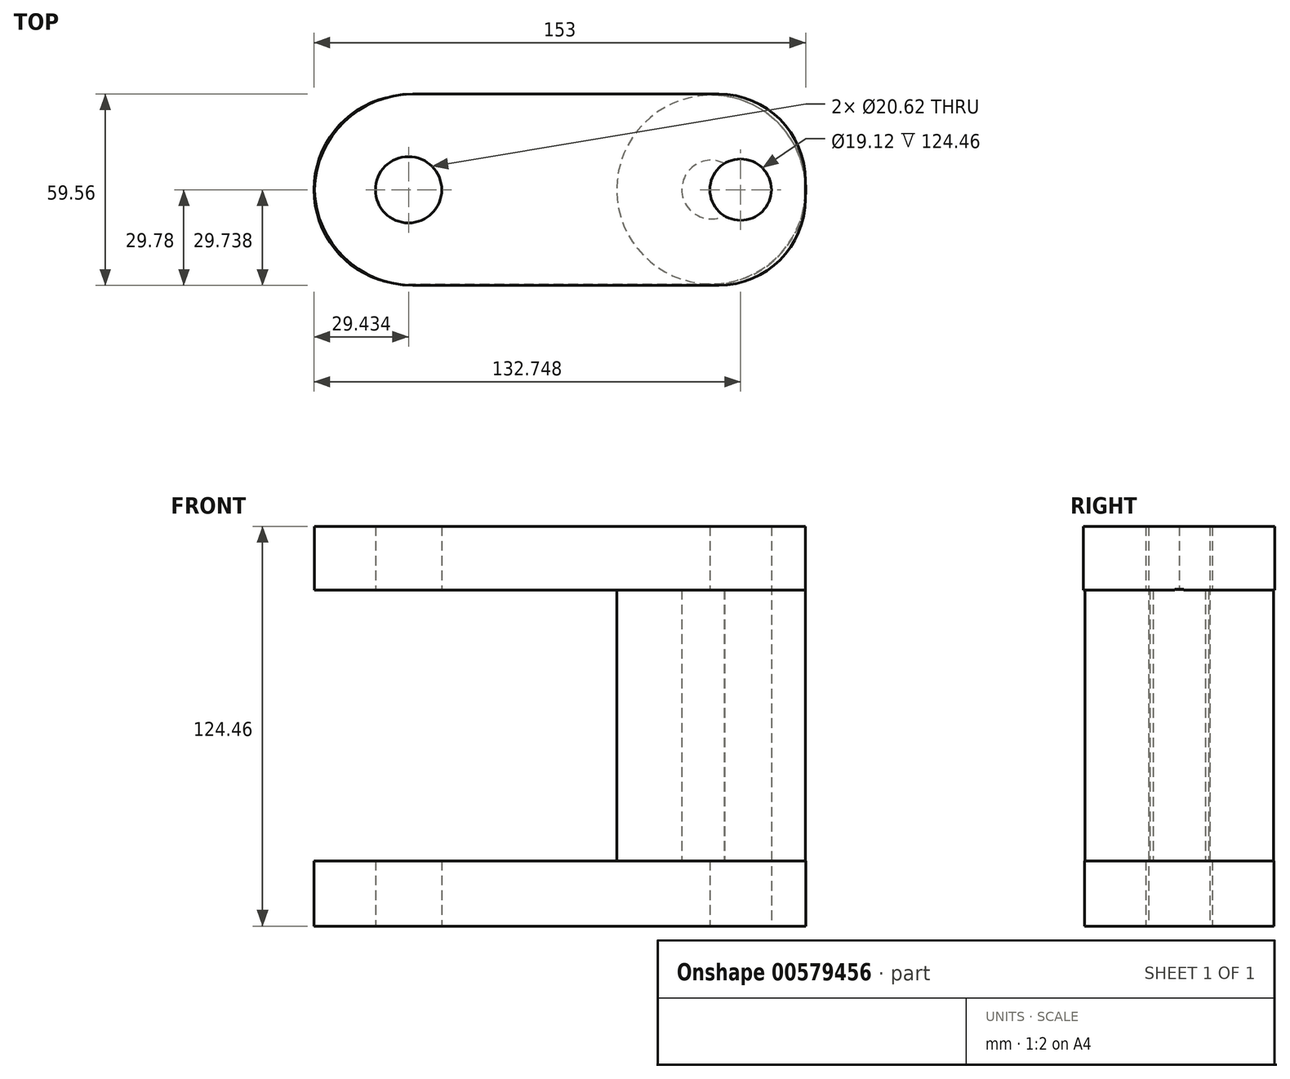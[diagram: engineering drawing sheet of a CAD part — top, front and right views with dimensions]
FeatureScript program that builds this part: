
annotation { "Feature Type Name" : "Feature", "Feature Type Description" : "" }
export const myFeature = defineFeature(function(context is Context, id is Id, definition is map)
    precondition{}
    {
        {
            var Q0;
            Q0=qCreatedBy(makeId("Top.planeOp"),FACE);
            var sketch = newSketch(context, id + "F0", { "sketchPlane" : qUnion([Q0])});
            skLineSegment(sketch, "E0.bottom", {"start": v(76.5, 29.48) * mm, "end": v(-76.5, 29.48) * mm});
            skLineSegment(sketch, "E0.top", {"start": v(76.5, -29.48) * mm, "end": v(-76.5, -29.48) * mm});
            skLineSegment(sketch, "E0.left", {"start": v(76.5, 29.48) * mm, "end": v(76.5, -29.48) * mm});
            skLineSegment(sketch, "E0.right", {"start": v(-76.5, 29.48) * mm, "end": v(-76.5, -29.48) * mm});
            skPoint(sketch, "E0.middle", {"position": v(0, 0) * mm});
            skSolve(sketch);
        }
        {
            var Q0;
            Q0 = qSketchRegion(id + "F0", true);
            extrude(context, id + "F1", {"entities" : qUnion([Q0]), "depth" : 20.32 * mm, "offsetDistance" : 25.4 * mm});
        }
        {
            var Q0;
            Q0=makeQuery(id+"F1.opExtrude","SWEPT_EDGE",EDGE,{"disambiguationData":[OSD([sQuery(id+"F0.wireOp",EDGE,"E0.top"),sQuery(id+"F0.wireOp",EDGE,"E0.right")])]});
            var Q1;
            Q1=makeQuery(id+"F1.opExtrude","SWEPT_EDGE",EDGE,{"disambiguationData":[OSD([sQuery(id+"F0.wireOp",EDGE,"E0.bottom"),sQuery(id+"F0.wireOp",EDGE,"E0.right")])]});
            var Q2;
            Q2=makeQuery(id+"F1.opExtrude","SWEPT_EDGE",EDGE,{"disambiguationData":[OSD([sQuery(id+"F0.wireOp",EDGE,"E0.top"),sQuery(id+"F0.wireOp",EDGE,"E0.left")])]});
            var Q3;
            Q3=makeQuery(id+"F1.opExtrude","SWEPT_EDGE",EDGE,{"disambiguationData":[OSD([sQuery(id+"F0.wireOp",EDGE,"E0.bottom"),sQuery(id+"F0.wireOp",EDGE,"E0.left")])]});
            fillet(context, id + "F2", {"entities" : qUnion([Q0, Q1, Q2, Q3]), "radius" : 29.43 * mm, "tangentPropagation" : true, "allowEdgeOverflow" : false});
        }
        {
            var Q0;
            Q0=makeQuery(id+"F1.opExtrude","CAP_FACE",FACE,{"disambiguationData":[OSD([sQuery(id+"F0.wireOp",EDGE,"E0.bottom"),sQuery(id+"F0.wireOp",EDGE,"E0.top"),sQuery(id+"F0.wireOp",EDGE,"E0.left"),sQuery(id+"F0.wireOp",EDGE,"E0.right")])],"isStart":false});
            var sketch = newSketch(context, id + "F3", { "sketchPlane" : qUnion([Q0])});
            skCircle(sketch, "E1", {"center": v(47.07, 0.04) * mm, "radius": 29.37 * mm});
            skCircle(sketch, "E2", {"center": v(47.07, 0.04) * mm, "radius": 9.12 * mm});
            skSolve(sketch);
        }
        {
            var Q0;
            Q0=makeQuery(id+"F3.imprint","IMPRINT",FACE,{"disambiguationData":[TD([[makeQuery(id+"F3.imprint","IMPRINT",EDGE,{"derivedFrom":sQuery(id+"F3.wireOp",EDGE,"E1")}),1.0]])]});
            extrude(context, id + "F4", {"entities" : qUnion([Q0]), "operationType" : NewBodyOperationType.ADD, "depth" : 84.58 * mm, "offsetDistance" : 25.4 * mm});
        }
        {
            var Q0;
            Q0=makeQuery(id+"F4.boolean.opBoolean","SPLIT",FACE,{"disambiguationData":[TD([makeQuery(id+"F4.opExtrude","SWEPT_FACE",FACE,{"disambiguationData":[OSD([sQuery(id+"F3.wireOp",EDGE,"E2")])]})])],"derivedFrom":makeQuery(id+"F1.opExtrude","CAP_FACE",FACE,{"disambiguationData":[OSD([sQuery(id+"F0.wireOp",EDGE,"E0.bottom"),sQuery(id+"F0.wireOp",EDGE,"E0.top"),sQuery(id+"F0.wireOp",EDGE,"E0.left"),sQuery(id+"F0.wireOp",EDGE,"E0.right")])],"isStart":false})});
            extrude(context, id + "F5", {"entities" : qUnion([Q0]), "operationType" : NewBodyOperationType.REMOVE, "endBound" : BoundingType.THROUGH_ALL, "depth" : 25.4 * mm, "offsetDistance" : 25.4 * mm});
        }
        {
            var Q0;
            {var subQ0=sQuery(id+"F0.wireOp",EDGE,"E0.left");var subQ1=sQuery(id+"F0.wireOp",EDGE,"E0.bottom");var subQ2=sQuery(id+"F0.wireOp",EDGE,"E0.top");var subQ3=sQuery(id+"F0.wireOp",EDGE,"E0.right");Q0=makeQuery(id+"F4.boolean.opBoolean","SPLIT",FACE,{"disambiguationData":[TD([makeQuery(id+"F1.opExtrude","SWEPT_FACE",FACE,{"disambiguationData":[OSD([subQ1])]})])],"derivedFrom":makeQuery(id+"F1.opExtrude","CAP_FACE",FACE,{"disambiguationData":[OSD([subQ1,subQ2,subQ0,subQ3])],"isStart":false})});}
            var sketch = newSketch(context, id + "F6", { "sketchPlane" : qUnion([Q0])});
            skCircle(sketch, "E3", {"center": v(-47.07, 0.04) * mm, "radius": 12.08 * mm});
            skSolve(sketch);
        }
        {
            var Q0;
            Q0=makeQuery(id+"F6.imprint","IMPRINT",FACE,{"disambiguationData":[TD([[makeQuery(id+"F6.imprint","IMPRINT",EDGE,{"derivedFrom":sQuery(id+"F6.wireOp",EDGE,"E3")}),1.0]])]});
            extrude(context, id + "F7", {"entities" : qUnion([Q0]), "operationType" : NewBodyOperationType.REMOVE, "endBound" : BoundingType.THROUGH_ALL, "depth" : 25.4 * mm, "offsetDistance" : 25.4 * mm});
        }
        {
            var Q0;
            Q0=qCreatedBy(makeId("Top.planeOp"),FACE);
            cPlane(context, id + "F8", {"entities" : qUnion([Q0]), "cplaneType" : CPlaneType.OFFSET, "offset" : 104.65 * mm, "width" : 152.4 * mm, "height" : 152.4 * mm});
        }
        {
            var Q0;
            Q0=qCreatedBy(id+"F8.planeOp",FACE);
            var sketch = newSketch(context, id + "F9", { "sketchPlane" : qUnion([Q0])});
            skLineSegment(sketch, "E4.bottom", {"start": v(76.4, -29.78) * mm, "end": v(-76.4, -29.78) * mm});
            skLineSegment(sketch, "E4.top", {"start": v(76.4, 29.78) * mm, "end": v(-76.4, 29.78) * mm});
            skLineSegment(sketch, "E4.left", {"start": v(76.4, -29.78) * mm, "end": v(76.4, 29.78) * mm});
            skLineSegment(sketch, "E4.right", {"start": v(-76.4, -29.78) * mm, "end": v(-76.4, 29.78) * mm});
            skPoint(sketch, "E4.middle", {"position": v(0, 0) * mm});
            skSolve(sketch);
        }
        {
            var Q0;
            Q0=makeQuery(id+"F9.imprint","IMPRINT",FACE,{"disambiguationData":[TD([[makeQuery(id+"F9.imprint","IMPRINT",EDGE,{"derivedFrom":sQuery(id+"F9.wireOp",EDGE,"E4.bottom")}),-1.0]])]});
            extrude(context, id + "F10", {"entities" : qUnion([Q0]), "operationType" : NewBodyOperationType.ADD, "depth" : 19.8 * mm, "offsetDistance" : 25.4 * mm});
        }
        {
            var Q0;
            Q0=makeQuery(id+"F1.opExtrude","CAP_FACE",FACE,{"disambiguationData":[OSD([sQuery(id+"F0.wireOp",EDGE,"E0.bottom"),sQuery(id+"F0.wireOp",EDGE,"E0.top"),sQuery(id+"F0.wireOp",EDGE,"E0.left"),sQuery(id+"F0.wireOp",EDGE,"E0.right")])],"isStart":true});
            var sketch = newSketch(context, id + "F11", { "sketchPlane" : qUnion([Q0])});
            skCircle(sketch, "E5", {"center": v(-47.07, 0.04) * mm, "radius": 10.31 * mm});
            skSolve(sketch);
        }
        {
            var Q0;
            Q0=makeQuery(id+"F11.imprint","IMPRINT",FACE,{"disambiguationData":[TD([[makeQuery(id+"F11.imprint","IMPRINT",EDGE,{"derivedFrom":sQuery(id+"F11.wireOp",EDGE,"E5")}),1.0]])]});
            extrude(context, id + "F12", {"entities" : qUnion([Q0]), "operationType" : NewBodyOperationType.REMOVE, "endBound" : BoundingType.THROUGH_ALL, "oppositeDirection" : true, "depth" : 25.4 * mm, "offsetDistance" : 25.4 * mm});
        }
        {
            var Q0;
            Q0=makeQuery(id+"F10.opExtrude","SWEPT_EDGE",EDGE,{"disambiguationData":[OSD([sQuery(id+"F9.wireOp",EDGE,"E4.bottom"),sQuery(id+"F9.wireOp",EDGE,"E4.right")])]});
            var Q1;
            Q1=makeQuery(id+"F10.opExtrude","SWEPT_EDGE",EDGE,{"disambiguationData":[OSD([sQuery(id+"F9.wireOp",EDGE,"E4.top"),sQuery(id+"F9.wireOp",EDGE,"E4.right")])]});
            fillet(context, id + "F13", {"entities" : qUnion([Q0, Q1]), "radius" : 30.66 * mm, "tangentPropagation" : true, "allowEdgeOverflow" : false});
        }
        {
            var Q0;
            Q0=makeQuery(id+"F10.opExtrude","SWEPT_EDGE",EDGE,{"disambiguationData":[OSD([sQuery(id+"F9.wireOp",EDGE,"E4.bottom"),sQuery(id+"F9.wireOp",EDGE,"E4.left")])]});
            var Q1;
            Q1=makeQuery(id+"F10.opExtrude","SWEPT_EDGE",EDGE,{"disambiguationData":[OSD([sQuery(id+"F9.wireOp",EDGE,"E4.top"),sQuery(id+"F9.wireOp",EDGE,"E4.left")])]});
            fillet(context, id + "F14", {"entities" : qUnion([Q0, Q1]), "radius" : 26.98 * mm, "tangentPropagation" : true, "allowEdgeOverflow" : false});
        }
        {
            var Q0;
            Q0=makeQuery(id+"F1.opExtrude","CAP_FACE",FACE,{"disambiguationData":[OSD([sQuery(id+"F0.wireOp",EDGE,"E0.bottom"),sQuery(id+"F0.wireOp",EDGE,"E0.top"),sQuery(id+"F0.wireOp",EDGE,"E0.left"),sQuery(id+"F0.wireOp",EDGE,"E0.right")])],"isStart":true});
            var sketch = newSketch(context, id + "F15", { "sketchPlane" : qUnion([Q0])});
            skCircle(sketch, "E6", {"center": v(56.25, 0) * mm, "radius": 9.56 * mm});
            skSolve(sketch);
        }
        {
            var Q0;
            Q0=makeQuery(id+"F15.imprint","IMPRINT",FACE,{"disambiguationData":[TD([[makeQuery(id+"F15.imprint","IMPRINT",EDGE,{"derivedFrom":sQuery(id+"F15.wireOp",EDGE,"E6")}),1.0]])]});
            extrude(context, id + "F16", {"entities" : qUnion([Q0]), "operationType" : NewBodyOperationType.REMOVE, "endBound" : BoundingType.THROUGH_ALL, "oppositeDirection" : true, "depth" : 25.4 * mm, "offsetDistance" : 25.4 * mm});
        }
    });
